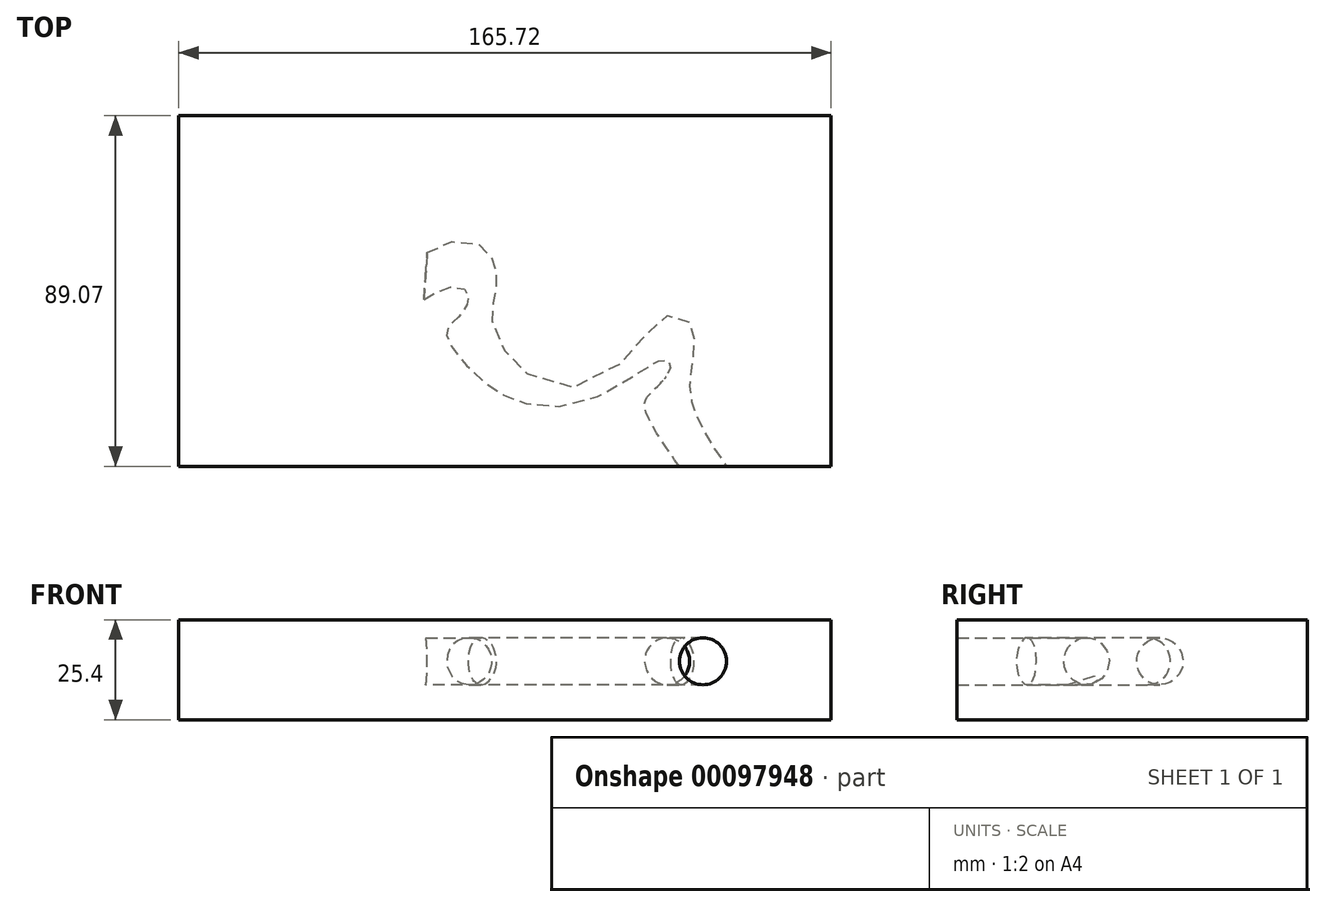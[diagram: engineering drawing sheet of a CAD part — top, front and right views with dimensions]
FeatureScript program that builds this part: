
annotation { "Feature Type Name" : "Feature", "Feature Type Description" : "" }
export const myFeature = defineFeature(function(context is Context, id is Id, definition is map)
    precondition{}
    {
        {
            var Q0;
            Q0=qCreatedBy(makeId("Top.planeOp"),FACE);
            var sketch = newSketch(context, id + "F0", { "sketchPlane" : qUnion([Q0])});
            skLineSegment(sketch, "E0.bottom", {"start": v(-23.13, 21.37) * mm, "end": v(142.59, 21.37) * mm});
            skLineSegment(sketch, "E0.top", {"start": v(-23.13, -67.7) * mm, "end": v(142.59, -67.7) * mm});
            skLineSegment(sketch, "E0.left", {"start": v(-23.13, 21.37) * mm, "end": v(-23.13, -67.7) * mm});
            skLineSegment(sketch, "E0.right", {"start": v(142.59, 21.37) * mm, "end": v(142.59, -67.7) * mm});
            skSolve(sketch);
        }
        {
            var Q0;
            Q0 = qSketchRegion(id + "F0", true);
            extrude(context, id + "F1", {"entities" : qUnion([Q0]), "depth" : 25.4 * mm});
        }
        {
            var Q0;
            Q0=makeQuery(id+"F1.opExtrude","SWEPT_FACE",FACE,{"disambiguationData":[OSD([sQuery(id+"F0.wireOp",EDGE,"E0.top")])]});
            var sketch = newSketch(context, id + "F2", { "sketchPlane" : qUnion([Q0])});
            skCircle(sketch, "E1", {"center": v(110.07, 14.87) * mm, "radius": 5.97 * mm});
            skSolve(sketch);
        }
        {
            var Q0;
            Q0=makeQuery(id+"F1.opExtrude","CAP_FACE",FACE,{"disambiguationData":[OSD([sQuery(id+"F0.wireOp",EDGE,"E0.bottom"),sQuery(id+"F0.wireOp",EDGE,"E0.top"),sQuery(id+"F0.wireOp",EDGE,"E0.left"),sQuery(id+"F0.wireOp",EDGE,"E0.right")])],"isStart":false});
            var sketch = newSketch(context, id + "F3", { "sketchPlane" : qUnion([Q0])});
            skFitSpline(sketch, "E2", {"points": [v(111.84, -46.81) * mm, v(88.65, -26.26) * mm, v(68.68, -31.14) * mm, v(43.24, -9.09) * mm, v(18.88, -16.14) * mm], "startDerivative": vector(-85.58, 115.4) * mm, "endDerivative": vector(-103.8, -66.1) * mm});
            skSolve(sketch);
        }
        {
            var Q0;
            Q0 = qSketchRegion(id + "F2", true);
            var Q1;
            Q1=sQuery(id+"F3.wireOp",EDGE,"E2");
            sweep(context, id + "F4", {"operationType" : NewBodyOperationType.REMOVE, "profiles" : qUnion([Q0]), "path" : qUnion([Q1])});
        }
    });
